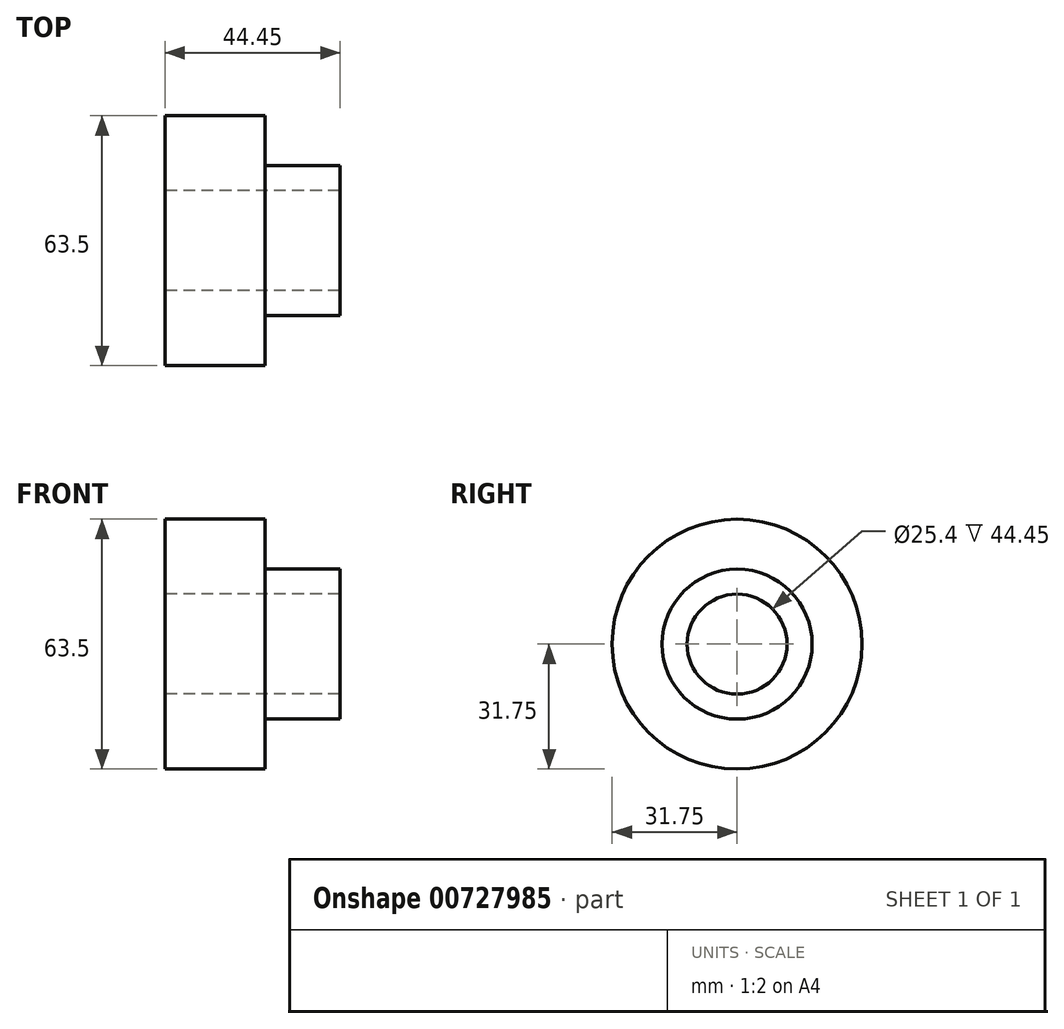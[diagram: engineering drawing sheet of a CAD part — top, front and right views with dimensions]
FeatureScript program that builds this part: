
annotation { "Feature Type Name" : "Feature", "Feature Type Description" : "" }
export const myFeature = defineFeature(function(context is Context, id is Id, definition is map)
    precondition{}
    {
        {
            var Q0;
            Q0=qCreatedBy(makeId("Right.planeOp"),FACE);
            var sketch = newSketch(context, id + "F0", { "sketchPlane" : qUnion([Q0])});
            skCircle(sketch, "E0", {"center": v(0, 0) * mm, "radius": 31.75 * mm});
            skSolve(sketch);
        }
        {
            var Q0;
            Q0=makeQuery(id+"F0.imprint","IMPRINT",FACE,{"disambiguationData":[TD([[makeQuery(id+"F0.imprint","IMPRINT",EDGE,{"derivedFrom":sQuery(id+"F0.wireOp",EDGE,"E0")}),1.0]])]});
            extrude(context, id + "F1", {"entities" : qUnion([Q0]), "depth" : 25.4 * mm, "offsetDistance" : 25.4 * mm});
        }
        {
            var Q0;
            Q0=qCreatedBy(makeId("Right.planeOp"),FACE);
            var sketch = newSketch(context, id + "F2", { "sketchPlane" : qUnion([Q0])});
            skCircle(sketch, "E1", {"center": v(0, 0) * mm, "radius": 19.05 * mm});
            skSolve(sketch);
        }
        {
            var Q0;
            Q0 = qSketchRegion(id + "F2", true);
            extrude(context, id + "F3", {"entities" : qUnion([Q0]), "operationType" : NewBodyOperationType.ADD, "depth" : 44.45 * mm, "offsetDistance" : 25.4 * mm});
        }
        {
            var Q0;
            Q0=qCreatedBy(makeId("Right.planeOp"),FACE);
            var sketch = newSketch(context, id + "F4", { "sketchPlane" : qUnion([Q0])});
            skCircle(sketch, "E2", {"center": v(0, 0) * mm, "radius": 12.7 * mm});
            skSolve(sketch);
        }
        {
            var Q0;
            Q0 = qSketchRegion(id + "F4", true);
            extrude(context, id + "F5", {"entities" : qUnion([Q0]), "operationType" : NewBodyOperationType.REMOVE, "depth" : 44.45 * mm, "offsetDistance" : 25.4 * mm});
        }
    });
